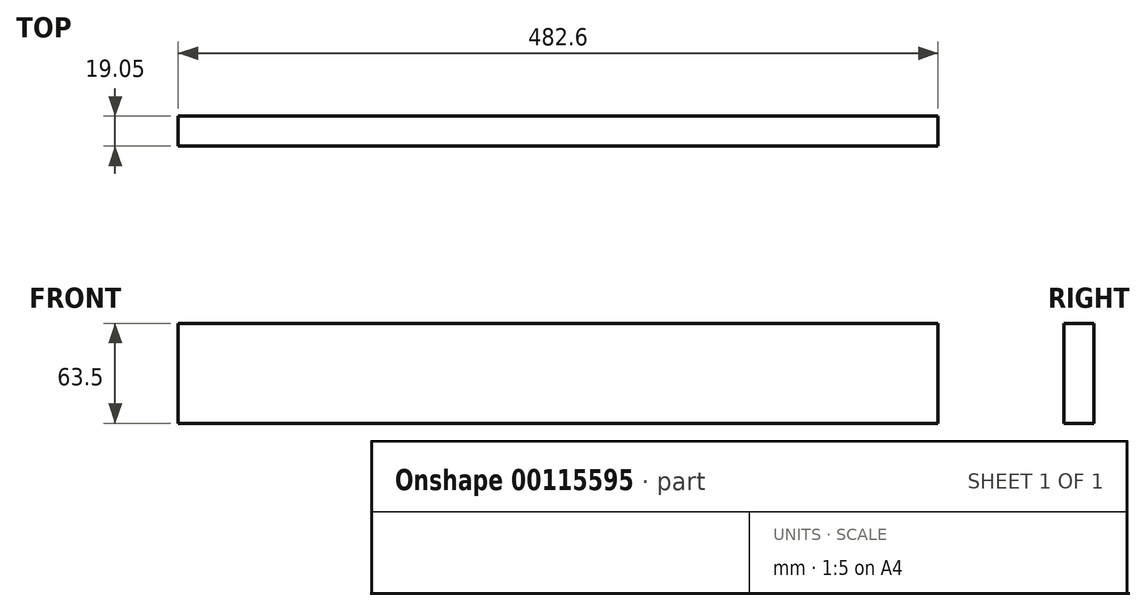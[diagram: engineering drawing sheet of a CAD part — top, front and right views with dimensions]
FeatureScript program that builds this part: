
annotation { "Feature Type Name" : "Feature", "Feature Type Description" : "" }
export const myFeature = defineFeature(function(context is Context, id is Id, definition is map)
    precondition{}
    {
        {
            var Q0;
            Q0=qCreatedBy(makeId("Front.planeOp"),FACE);
            var sketch = newSketch(context, id + "F0", { "sketchPlane" : qUnion([Q0])});
            skLineSegment(sketch, "E0.bottom", {"start": v(-241.3, 31.75) * mm, "end": v(241.3, 31.75) * mm});
            skLineSegment(sketch, "E0.top", {"start": v(-241.3, -31.75) * mm, "end": v(241.3, -31.75) * mm});
            skLineSegment(sketch, "E0.left", {"start": v(-241.3, 31.75) * mm, "end": v(-241.3, -31.75) * mm});
            skLineSegment(sketch, "E0.right", {"start": v(241.3, 31.75) * mm, "end": v(241.3, -31.75) * mm});
            skPoint(sketch, "E0.middle", {"position": v(0, 0) * mm});
            skSolve(sketch);
        }
        {
            var Q0;
            Q0=makeQuery(id+"F0.imprint","IMPRINT",FACE,{"disambiguationData":[TD([[makeQuery(id+"F0.imprint","IMPRINT",EDGE,{"derivedFrom":sQuery(id+"F0.wireOp",EDGE,"E0.bottom")}),-1.0]])]});
            extrude(context, id + "F1", {"entities" : qUnion([Q0]), "depth" : 19.05 * mm});
        }
    });
